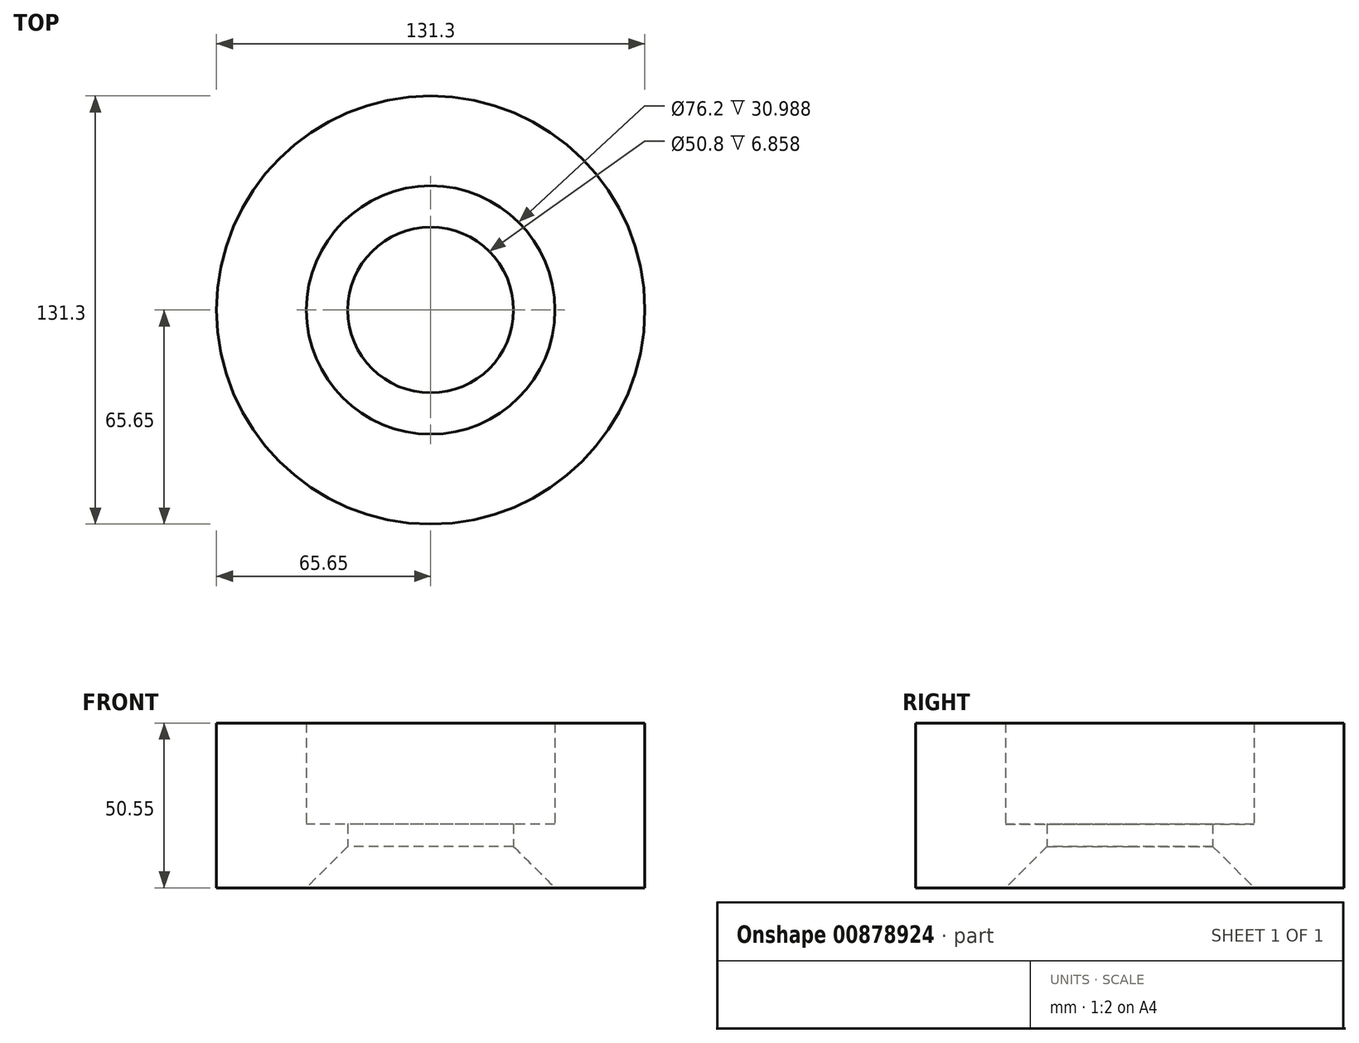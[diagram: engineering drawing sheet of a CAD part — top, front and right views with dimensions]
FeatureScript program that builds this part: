
annotation { "Feature Type Name" : "Feature", "Feature Type Description" : "" }
export const myFeature = defineFeature(function(context is Context, id is Id, definition is map)
    precondition{}
    {
        {
            var Q0;
            Q0=qCreatedBy(makeId("Top.planeOp"),FACE);
            var sketch = newSketch(context, id + "F0", { "sketchPlane" : qUnion([Q0])});
            skCircle(sketch, "E0", {"center": v(0, 0) * mm, "radius": 65.65 * mm});
            skCircle(sketch, "E1", {"center": v(0, 0) * mm, "radius": 25.4 * mm});
            skCircle(sketch, "E2", {"center": v(0, 0) * mm, "radius": 38.1 * mm});
            skSolve(sketch);
        }
        {
            var Q0;
            Q0=makeQuery(id+"F0.imprint","IMPRINT",FACE,{"disambiguationData":[TD([[makeQuery(id+"F0.imprint","IMPRINT",EDGE,{"derivedFrom":sQuery(id+"F0.wireOp",EDGE,"E0")}),1.0]])]});
            extrude(context, id + "F1", {"entities" : qUnion([Q0]), "depth" : 50.55 * mm, "offsetDistance" : 25.4 * mm});
        }
        {
            var Q0;
            Q0=makeQuery(id+"F0.imprint","IMPRINT",FACE,{"disambiguationData":[TD([[makeQuery(id+"F0.imprint","IMPRINT",EDGE,{"derivedFrom":sQuery(id+"F0.wireOp",EDGE,"E1")}),-1.0]])]});
            extrude(context, id + "F2", {"entities" : qUnion([Q0]), "operationType" : NewBodyOperationType.ADD, "depth" : 19.56 * mm, "offsetDistance" : 25.4 * mm});
        }
        {
            var Q0;
            Q0=makeQuery(id+"F2.opExtrude","CAP_EDGE",EDGE,{"disambiguationData":[OSD([sQuery(id+"F0.wireOp",EDGE,"E1")])],"isStart":true});
            chamfer(context, id + "F3", {"entities" : qUnion([Q0]), "width" : 12.7 * mm, "tangentPropagation" : true});
        }
    });
